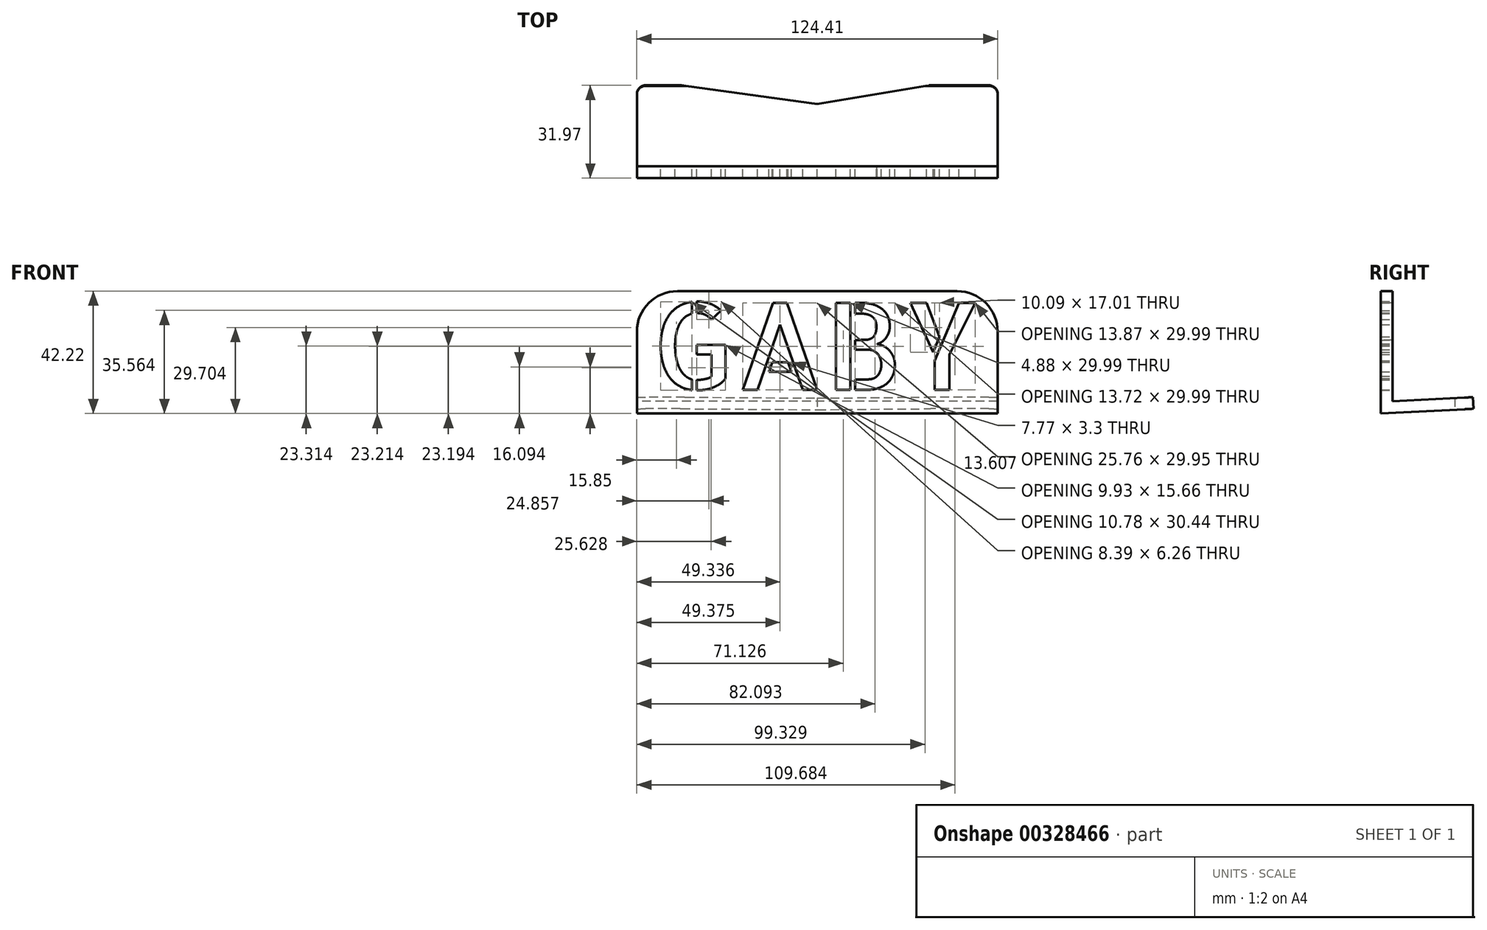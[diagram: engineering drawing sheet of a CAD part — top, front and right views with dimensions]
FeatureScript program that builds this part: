
annotation { "Feature Type Name" : "Feature", "Feature Type Description" : "" }
export const myFeature = defineFeature(function(context is Context, id is Id, definition is map)
    precondition{}
    {
        {
            var Q0;
            Q0=qCreatedBy(makeId("Front.planeOp"),FACE);
            var sketch = newSketch(context, id + "F0", { "sketchPlane" : qUnion([Q0])});
            skText(sketch, "E0", { "text": "GABY", "fontName": "AllertaStencil-Regular.ttf"});
            skLineSegment(sketch, "E1.bottom", {"start": v(7.58, 61.62) * mm, "end": v(132, 61.62) * mm});
            skLineSegment(sketch, "E1.top", {"start": v(7.58, 23.62) * mm, "end": v(132, 23.62) * mm});
            skLineSegment(sketch, "E1.left", {"start": v(7.58, 61.62) * mm, "end": v(7.58, 23.62) * mm});
            skLineSegment(sketch, "E1.right", {"start": v(132, 61.62) * mm, "end": v(132, 23.62) * mm});
            skPoint(sketch, "E2", {"position": v(127, 42.62) * mm});
            skPoint(sketch, "E3", {"position": v(132, 42.62) * mm});
            skPoint(sketch, "E4", {"position": v(69.79, 61.62) * mm});
            skLineSegment(sketch, "E5", {"start": v(7.58, 27.12) * mm, "end": v(132, 27.12) * mm});
            const initialGuessF0  = {"E0": [0.01258, 0.02762, 1, 0, 0.03]};
            skSetInitialGuess(sketch, initialGuessF0);
            skSolve(sketch);
        }
        {
            var Q0;
            Q0=makeQuery(id+"F0.imprint","IMPRINT",FACE,{"disambiguationData":[TD([[makeQuery(id+"F0.imprint","IMPRINT",EDGE,{"derivedFrom":sQuery(id+"F0.wireOp",EDGE,"E0.sketch_text.stroke-0")}),1.0]])]});
            extrude(context, id + "F1", {"entities" : qUnion([Q0]), "depth" : 4 * mm});
        }
        {
            var Q0;
            Q0=qCreatedBy(makeId("Right.planeOp"),FACE);
            var sketch = newSketch(context, id + "F2", { "sketchPlane" : qUnion([Q0])});
            skLineSegment(sketch, "E6", {"start": v(27.76, 25.07) * mm, "end": v(0, 23.62) * mm});
            skLineSegment(sketch, "E7", {"start": v(27.76, 25.07) * mm, "end": v(27.97, 21.08) * mm});
            skLineSegment(sketch, "E8", {"start": v(27.97, 21.08) * mm, "end": v(-4, 19.4) * mm});
            skPoint(sketch, "E9", {"position": v(-4, 27.12) * mm});
            skLineSegment(sketch, "E10", {"start": v(-4, 27.12) * mm, "end": v(-4, 19.4) * mm});
            skLineSegment(sketch, "E11", {"start": v(0, 23.62) * mm, "end": v(0, 27.12) * mm});
            skLineSegment(sketch, "E12", {"start": v(0, 27.12) * mm, "end": v(-4, 27.12) * mm});
            skSolve(sketch);
        }
        {
            var Q0;
            Q0=makeQuery(id+"F2.imprint","IMPRINT",FACE,{"disambiguationData":[TD([[makeQuery(id+"F2.imprint","IMPRINT",EDGE,{"derivedFrom":sQuery(id+"F2.wireOp",EDGE,"E6")}),1.0]])]});
            var Q1;
            Q1=makeQuery(id+"F1.opExtrude","CAP_VERTEX",VERTEX,{"disambiguationData":[OSD([sQuery(id+"F0.wireOp",EDGE,"E1.right"),sQuery(id+"F0.wireOp",EDGE,"E5")])],"isStart":false});
            var Q2;
            Q2=makeQuery(id+"F1.opExtrude","CAP_VERTEX",VERTEX,{"disambiguationData":[OSD([sQuery(id+"F0.wireOp",EDGE,"E1.left"),sQuery(id+"F0.wireOp",EDGE,"E5")])],"isStart":false});
            extrude(context, id + "F3", {"entities" : qUnion([Q0]), "operationType" : NewBodyOperationType.ADD, "endBound" : BoundingType.UP_TO_VERTEX, "endBoundEntityVertex" : qUnion([Q1]), "depth" : 25 * mm, "hasSecondDirection" : true, "secondDirectionBound" : SecondDirectionBoundingType.UP_TO_VERTEX, "secondDirectionOppositeDirection" : false, "secondDirectionBoundEntityVertex" : qUnion([Q2]), "secondDirectionDepth" : 25 * mm});
        }
        {
            var Q0;
            Q0=makeQuery(id+"F1.opExtrude","SWEPT_EDGE",EDGE,{"disambiguationData":[OSD([sQuery(id+"F0.wireOp",EDGE,"E1.bottom"),sQuery(id+"F0.wireOp",EDGE,"E1.left")])]});
            var Q1;
            Q1=makeQuery(id+"F1.opExtrude","SWEPT_EDGE",EDGE,{"disambiguationData":[OSD([sQuery(id+"F0.wireOp",EDGE,"E1.bottom"),sQuery(id+"F0.wireOp",EDGE,"E1.right")])]});
            fillet(context, id + "F4", {"entities" : qUnion([Q0, Q1]), "radius" : 14 * mm, "tangentPropagation" : true, "allowEdgeOverflow" : false});
        }
        {
            var Q0;
            Q0=qCreatedBy(makeId("Top.planeOp"),FACE);
            var sketch = newSketch(context, id + "F5", { "sketchPlane" : qUnion([Q0])});
            skLineSegment(sketch, "E13", {"start": v(22.76, 27.97) * mm, "end": v(69.79, 21.52) * mm});
            skLineSegment(sketch, "E14", {"start": v(69.79, 21.52) * mm, "end": v(108.57, 27.97) * mm});
            skLineSegment(sketch, "E15", {"start": v(108.57, 27.97) * mm, "end": v(22.76, 27.97) * mm});
            skPoint(sketch, "E16", {"position": v(69.79, -4) * mm});
            skSolve(sketch);
        }
        {
            var Q0;
            Q0=makeQuery(id+"F5.imprint","IMPRINT",FACE,{"disambiguationData":[TD([[makeQuery(id+"F5.imprint","IMPRINT",EDGE,{"derivedFrom":sQuery(id+"F5.wireOp",EDGE,"E13")}),1.0]])]});
            extrude(context, id + "F6", {"entities" : qUnion([Q0]), "operationType" : NewBodyOperationType.REMOVE, "depth" : 35.3 * mm});
        }
        {
            var Q0;
            Q0=makeQuery(id+"F6.boolean.opBoolean","INTERSECT",EDGE,{"derivedFrom":[makeQuery(id+"F3.opExtrude","SWEPT_FACE",FACE,{"disambiguationData":[OSD([sQuery(id+"F2.wireOp",EDGE,"E7")])]}),makeQuery(id+"F6.opExtrude","SWEPT_FACE",FACE,{"disambiguationData":[OSD([sQuery(id+"F5.wireOp",EDGE,"E14")])]})]});
            var Q1;
            Q1=makeQuery(id+"F6.boolean.opBoolean","INTERSECT",EDGE,{"derivedFrom":[makeQuery(id+"F3.opExtrude","SWEPT_FACE",FACE,{"disambiguationData":[OSD([sQuery(id+"F2.wireOp",EDGE,"E7")])]}),makeQuery(id+"F6.opExtrude","SWEPT_FACE",FACE,{"disambiguationData":[OSD([sQuery(id+"F5.wireOp",EDGE,"E13")])]})]});
            var Q2;
            Q2=makeQuery(id+"F3.opExtrude","CAP_EDGE",EDGE,{"disambiguationData":[OSD([sQuery(id+"F2.wireOp",EDGE,"E7")])],"isStart":true});
            var Q3;
            Q3=makeQuery(id+"F3.opExtrude","CAP_EDGE",EDGE,{"disambiguationData":[OSD([sQuery(id+"F2.wireOp",EDGE,"E7")])],"isStart":false});
            fillet(context, id + "F7", {"entities" : qUnion([Q0, Q1, Q2, Q3]), "radius" : 3 * mm, "tangentPropagation" : true, "allowEdgeOverflow" : false});
        }
    });
